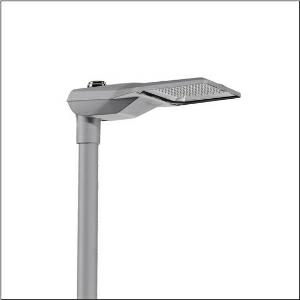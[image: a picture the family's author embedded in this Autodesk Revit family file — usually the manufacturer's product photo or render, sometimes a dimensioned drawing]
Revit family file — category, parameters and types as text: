
# Revit family: streetlight_sl_21_midi___stw1_0a_5xe7e37n08lb_0f97
name_source: partatom
category: Lighting Fixtures
units: mm (PartAtom-declared; Revit-internal decimal feet)

## family parameters
Cut with Voids When Loaded = No
Host = Face
Light Source = No
Part Type = Normal
Room Calculation Point = No
Round Connector Dimension = Use Diameter
Shared = No

## types (1)
- --- (1 x LED, 14340 lm, 98.3 W, 3000K)
    Apparent Load = 98 VA
    CIE Flux Codes = 38 75 98 100 100
    Color Rendering = 70
    Color Temperature = 3000K
    Default Elevation = 1800 mm
    Description = Streetlight SL 21 midi, mast luminaire, primary light control with lens, of PMMA, primary optical cover: cover, of toughened safety glass, transparent, light distribution: STW1.0a, light emission: direct distribution, primary light characteristic: asymmetric, installation type: side-entry, LED, 3G 2.5mm², High Power LED, rated luminous flux: 14.340lm, luminous efficacy: 146lm/W, light colour: 730, colour temperature: 3000K, control gear: NEMA (7pin), control: overheat protection, pre-setting: linear dimming characteristic, constant luminous flux control, time-dependent luminous flux control, flexible luminous flux parameterisation, mains connection: 220..240V, AC, 50/60Hz, connection cable pre-assembled, cable length: 10,5m, wiring characteristics: H05VV-F, start of lifetime: 98W, end of service life: 101W, reduction: 45W, luminaire housing, of diecast aluminium (EN AC-44300), powder-coated, SITECO metallic grey (DB 702S), corrosivity category C5 high according to DIN EN ISO 12944, multi-level sealing system, sealing non-destructively replaceable, inclination adjustable: 0°, 5°, 10°, 15°, length: 644mm, width: 335mm, height: 110mm, spigot size: 42mm (side-entry), mounting height: 4..8m, protection rating (complete): IP66, insulation class (complete): insulation class I (protective earthing), certification: CE, ENEC, ENEC+, VDE, impact resistance: IK10, permissible operating ambient temperature for outdoor applications: -40..+50°C, standard-compliant lighting for roads and squares, packaging unit: 1 piece

Light Distribution: STW1.0a
    Height = 111 mm
    Lamp = 1 x LED
    Lamp Light Flux = 14340 lm
    Lamp Power = 98.3 W
    Lamp count = 1
    Length = 644 mm
    Luminous efficacy = 146 lm/W
    Manufacturer = Siteco
    ModVariant = No
    Model = 5XE7E37N08LB
    Number of Poles = 1
    OnlyDefault = Yes
    Power Factor = 1
    Product Name = Streetlight SL 21 midi | STW1.0a
    Product group = mast luminaire | pylon top
    ProductGroupID = 6100
    Protection Class = Protection class I
    Protection Degree = IP 66
    RLX_Detail_Level = 1
    RLX_Emergency_Light_Flux = 0 lm
    RLX_Emergency_Type = 0
    RLX_Emergency_Type_DB = No
    RlxData = <blob elided: 26769 chars, md5=f2cc2de6>
    Socket = socket
    Standby Power = 0 W
    System Light Flux = 14340 lm
    System Power = 98 W
    Type Comments = factory setting: luminous flux: 100 % | dim-lin: 254 | 1020 mA
    Type Image = l_1294377.jpg
    URL = http://relux.com
    VarID = @adj_135053
    Voltage = 0 V
    Weight = 0.00 kg
    Width = 336 mm

## geometry (parser evidence)
native form markers: Blend x4, Sweep x9
no freeform markers — native parametric forms only
